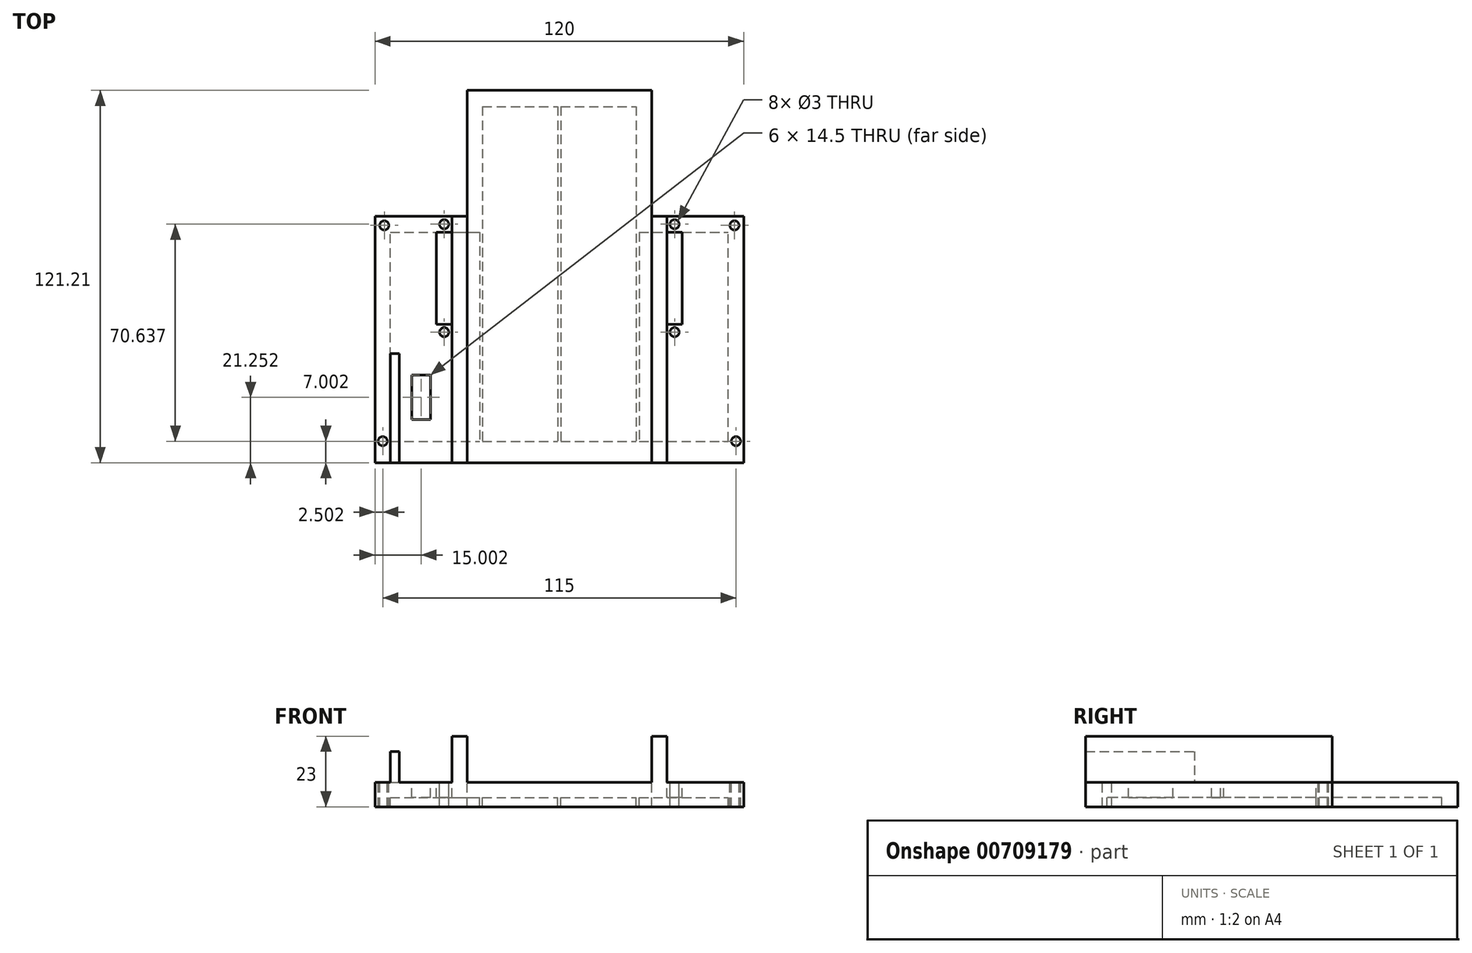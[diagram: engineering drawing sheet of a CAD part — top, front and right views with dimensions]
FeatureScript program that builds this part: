
annotation { "Feature Type Name" : "Feature", "Feature Type Description" : "" }
export const myFeature = defineFeature(function(context is Context, id is Id, definition is map)
    precondition{}
    {
        {
            var Q0;
            Q0=qCreatedBy(makeId("Top.planeOp"),FACE);
            var sketch = newSketch(context, id + "F0", { "sketchPlane" : qUnion([Q0])});
            skLineSegment(sketch, "E0.bottom", {"start": v(-56.52, -50.08) * mm, "end": v(53.48, -50.08) * mm});
            skLineSegment(sketch, "E0.top", {"start": v(-56.52, 17.92) * mm, "end": v(-26.52, 17.92) * mm});
            skLineSegment(sketch, "E0.left", {"start": v(-56.52, -50.08) * mm, "end": v(-56.52, 17.92) * mm});
            skLineSegment(sketch, "E0.right", {"start": v(53.48, -50.08) * mm, "end": v(53.48, 17.92) * mm});
            skLineSegment(sketch, "E1.bottom", {"start": v(-26.52, 58.85) * mm, "end": v(23.48, 58.85) * mm});
            skLineSegment(sketch, "E1.left", {"start": v(-26.52, 58.85) * mm, "end": v(-26.52, 17.92) * mm});
            skLineSegment(sketch, "E1.right", {"start": v(23.48, 58.85) * mm, "end": v(23.48, 17.92) * mm});
            skLineSegment(sketch, "E2.trimOffspring", {"start": v(23.48, 17.92) * mm, "end": v(53.48, 17.92) * mm});
            skCircle(sketch, "E3", {"center": v(55.98, -50.08) * mm, "radius": 1.5 * mm});
            skCircle(sketch, "E4", {"center": v(-59.02, -50.08) * mm, "radius": 1.5 * mm});
            skCircle(sketch, "E5", {"center": v(55.48, 20.18) * mm, "radius": 1.5 * mm});
            skCircle(sketch, "E6", {"center": v(-58.5, 20.19) * mm, "radius": 1.5 * mm});
            skLineSegment(sketch, "E7", {"start": v(-61.52, 23.2) * mm, "end": v(-61.52, -57.08) * mm});
            skLineSegment(sketch, "E8", {"start": v(-61.52, -57.08) * mm, "end": v(58.48, -57.08) * mm});
            skLineSegment(sketch, "E9", {"start": v(58.48, -57.08) * mm, "end": v(58.48, 23.2) * mm});
            skLineSegment(sketch, "E10", {"start": v(58.48, 23.2) * mm, "end": v(28.48, 23.2) * mm});
            skLineSegment(sketch, "E11", {"start": v(28.48, 64.13) * mm, "end": v(-31.52, 64.13) * mm});
            skLineSegment(sketch, "E12", {"start": v(-31.52, 64.13) * mm, "end": v(-31.52, 23.2) * mm});
            skLineSegment(sketch, "E13", {"start": v(-31.52, 23.2) * mm, "end": v(-61.52, 23.2) * mm});
            skLineSegment(sketch, "E14", {"start": v(-31.52, 23.2) * mm, "end": v(-31.52, -57.08) * mm});
            skLineSegment(sketch, "E15", {"start": v(28.48, 23.2) * mm, "end": v(28.48, -57.08) * mm});
            skLineSegment(sketch, "E16", {"start": v(-36.52, 23.2) * mm, "end": v(-36.52, -57.08) * mm});
            skLineSegment(sketch, "E17", {"start": v(-36.52, -57.08) * mm, "end": v(-31.52, -57.08) * mm});
            skLineSegment(sketch, "E18", {"start": v(-36.52, 23.2) * mm, "end": v(-31.52, 23.2) * mm});
            skLineSegment(sketch, "E19", {"start": v(33.48, 23.2) * mm, "end": v(33.48, -57.08) * mm});
            skLineSegment(sketch, "E20", {"start": v(33.48, -57.08) * mm, "end": v(28.48, -57.08) * mm});
            skLineSegment(sketch, "E21.bottom", {"start": v(-43.52, -43.08) * mm, "end": v(-49.52, -43.08) * mm});
            skLineSegment(sketch, "E21.top", {"start": v(-43.52, -28.58) * mm, "end": v(-49.52, -28.58) * mm});
            skLineSegment(sketch, "E21.left", {"start": v(-43.52, -43.08) * mm, "end": v(-43.52, -28.58) * mm});
            skLineSegment(sketch, "E21.right", {"start": v(-49.52, -43.08) * mm, "end": v(-49.52, -28.58) * mm});
            skLineSegment(sketch, "E22.bottom", {"start": v(-56.52, -50.08) * mm, "end": v(-53.58, -50.08) * mm});
            skLineSegment(sketch, "E22.top", {"start": v(-56.52, -21.58) * mm, "end": v(-53.58, -21.58) * mm});
            skLineSegment(sketch, "E22.left", {"start": v(-56.52, -50.08) * mm, "end": v(-56.52, -21.58) * mm});
            skLineSegment(sketch, "E22.right", {"start": v(-53.58, -50.08) * mm, "end": v(-53.58, -21.58) * mm});
            skLineSegment(sketch, "E23", {"start": v(-53.58, -50.08) * mm, "end": v(-53.58, -57.08) * mm});
            skLineSegment(sketch, "E24", {"start": v(-56.52, -50.08) * mm, "end": v(-56.52, -57.08) * mm});
            skLineSegment(sketch, "E25", {"start": v(-53.58, -57.08) * mm, "end": v(-56.52, -57.08) * mm});
            skLineSegment(sketch, "E26.bottom", {"start": v(23.48, 17.92) * mm, "end": v(24.48, 17.92) * mm});
            skLineSegment(sketch, "E26.top", {"start": v(23.48, -50.08) * mm, "end": v(24.48, -50.08) * mm});
            skLineSegment(sketch, "E26.left", {"start": v(23.48, 17.92) * mm, "end": v(23.48, -50.08) * mm});
            skLineSegment(sketch, "E26.right", {"start": v(24.48, 17.92) * mm, "end": v(24.48, -50.08) * mm});
            skLineSegment(sketch, "E27.left", {"start": v(24.48, -50.08) * mm, "end": v(24.48, 17.92) * mm});
            skLineSegment(sketch, "E28.bottom", {"start": v(-26.52, 17.92) * mm, "end": v(-27.52, 17.92) * mm});
            skLineSegment(sketch, "E28.top", {"start": v(-26.52, -50.08) * mm, "end": v(-27.52, -50.08) * mm});
            skLineSegment(sketch, "E28.left", {"start": v(-26.52, 17.92) * mm, "end": v(-26.52, -50.08) * mm});
            skLineSegment(sketch, "E28.right", {"start": v(-27.52, 17.92) * mm, "end": v(-27.52, -50.08) * mm});
            skLineSegment(sketch, "E29", {"start": v(-1.52, 58.85) * mm, "end": v(-2.02, 58.85) * mm});
            skLineSegment(sketch, "E30", {"start": v(-2.02, 58.85) * mm, "end": v(-2.02, -50.08) * mm});
            skLineSegment(sketch, "E31.MirrorCS", {"start": v(-1.02, 58.85) * mm, "end": v(-1.02, -50.08) * mm});
            skLineSegment(sketch, "E32.bottom", {"start": v(33.48, 23.2) * mm, "end": v(28.48, 23.2) * mm});
            skLineSegment(sketch, "E32.right", {"start": v(28.48, 23.2) * mm, "end": v(28.48, 64.13) * mm});
            skLineSegment(sketch, "E33.bottom", {"start": v(38.48, 17.92) * mm, "end": v(33.48, 17.92) * mm});
            skLineSegment(sketch, "E33.top", {"start": v(38.48, -12.08) * mm, "end": v(33.48, -12.08) * mm});
            skLineSegment(sketch, "E33.left", {"start": v(38.48, 17.92) * mm, "end": v(38.48, -12.08) * mm});
            skLineSegment(sketch, "E33.right", {"start": v(33.48, 17.92) * mm, "end": v(33.48, -12.08) * mm});
            skLineSegment(sketch, "E34.right", {"start": v(33.48, 17.92) * mm, "end": v(33.48, 23.2) * mm});
            skLineSegment(sketch, "E35.right", {"start": v(33.48, -12.08) * mm, "end": v(33.48, -17.08) * mm});
            skPoint(sketch, "E36", {"position": v(35.98, 20.56) * mm});
            skPoint(sketch, "E37", {"position": v(35.98, -14.58) * mm});
            skPoint(sketch, "E38.MirrorP", {"position": v(-39.02, -14.58) * mm});
            skPoint(sketch, "E39.MirrorP", {"position": v(-39.02, 20.56) * mm});
            skLineSegment(sketch, "E40.MirrorCS", {"start": v(-41.52, 17.92) * mm, "end": v(-41.52, -12.08) * mm});
            skLineSegment(sketch, "E41.MirrorCS", {"start": v(-41.52, -12.08) * mm, "end": v(-36.52, -12.08) * mm});
            skSolve(sketch);
        }
        {
            var Q0;
            {var subQ0=sQuery(id+"F0.wireOp",EDGE,"E28.right");var subQ6=sQuery(id+"F0.wireOp",EDGE,"E26.right");Q0=qUnion([makeQuery(id+"F0.imprint","IMPRINT",FACE,{"disambiguationData":[TD([[makeQuery(id+"F0.imprint","IMPRINT",EDGE,{"derivedFrom":subQ6}),1.0]])]}),makeQuery(id+"F0.imprint","IMPRINT",FACE,{"disambiguationData":[TD([[makeQuery(id+"F0.imprint","IMPRINT",EDGE,{"derivedFrom":subQ0}),-1.0]])]})]);}
            var Q1;
            Q1=makeQuery(id+"F0.imprint","IMPRINT",FACE,{"disambiguationData":[TD([[makeQuery(id+"F0.imprint","IMPRINT",EDGE,{"derivedFrom":sQuery(id+"F0.wireOp",EDGE,"E21.bottom")}),1.0]])]});
            var Q2;
            {var subQ4=sQuery(id+"F0.wireOp",EDGE,"E22.top");Q2=makeQuery(id+"F0.imprint","IMPRINT",FACE,{"disambiguationData":[TD([[makeQuery(id+"F0.imprint","IMPRINT",EDGE,{"derivedFrom":subQ4}),-1.0]])]});}
            var Q3;
            {var subQ0=sQuery(id+"F0.wireOp",EDGE,"E28.left");Q3=makeQuery(id+"F0.imprint","IMPRINT",FACE,{"disambiguationData":[TD([[makeQuery(id+"F0.imprint","IMPRINT",EDGE,{"derivedFrom":subQ0}),-1.0]])]});}
            var Q4;
            {var subQ0=sQuery(id+"F0.wireOp",EDGE,"E1.left");var subQ2=sQuery(id+"F0.wireOp",EDGE,"E30");var subQ7=makeQuery(id+"F0.imprint","IMPRINT",EDGE,{"derivedFrom":subQ2});var subQ9=sQuery(id+"F0.wireOp",EDGE,"E1.right");Q4=qUnion([makeQuery(id+"F0.imprint","IMPRINT",FACE,{"disambiguationData":[TD([[subQ7,1.0]])]}),makeQuery(id+"F0.imprint","IMPRINT",FACE,{"disambiguationData":[TD([[makeQuery(id+"F0.imprint","IMPRINT",EDGE,{"derivedFrom":subQ9}),-1.0]])]}),makeQuery(id+"F0.imprint","IMPRINT",FACE,{"disambiguationData":[TD([[makeQuery(id+"F0.imprint","IMPRINT",EDGE,{"derivedFrom":subQ0}),1.0]])]})]);}
            var Q5;
            {var subQ0=sQuery(id+"F0.wireOp",EDGE,"E26.left");Q5=makeQuery(id+"F0.imprint","IMPRINT",FACE,{"disambiguationData":[TD([[makeQuery(id+"F0.imprint","IMPRINT",EDGE,{"derivedFrom":subQ0}),1.0]])]});}
            var Q6;
            {var subQ5=sQuery(id+"F0.wireOp",EDGE,"E0.right");Q6=makeQuery(id+"F0.imprint","IMPRINT",FACE,{"disambiguationData":[TD([[makeQuery(id+"F0.imprint","IMPRINT",EDGE,{"derivedFrom":subQ5}),1.0]])]});}
            var Q7;
            {var subQ0=sQuery(id+"F0.wireOp",EDGE,"E19");var subQ1=makeQuery(id+"F0.imprint","IMPRINT",VERTEX,{"derivedFrom":subQ0});Q7=makeQuery(id+"F0.imprint","IMPRINT",FACE,{"disambiguationData":[TD([[makeQuery(id+"F0.imprint","IMPRINT",EDGE,{"disambiguationData":[TD([[subQ1,-1.0]])],"derivedFrom":subQ0}),-1.0]])]});}
            var Q8;
            Q8=makeQuery(id+"F0.imprint","IMPRINT",FACE,{"disambiguationData":[TD([[makeQuery(id+"F0.imprint","IMPRINT",EDGE,{"derivedFrom":sQuery(id+"F0.wireOp",EDGE,"E33.bottom")}),1.0]])]});
            var Q9;
            {var subQ0=sQuery(id+"F0.wireOp",EDGE,"E16");var subQ2=sQuery(id+"F0.wireOp",EDGE,"E0.bottom");var subQ3=makeQuery(id+"F0.imprint","INTERSECT",VERTEX,{"derivedFrom":[subQ2,subQ0]});Q9=makeQuery(id+"F0.imprint","IMPRINT",FACE,{"disambiguationData":[TD([[makeQuery(id+"F0.imprint","IMPRINT",EDGE,{"disambiguationData":[TD([[subQ3,-1.0]])],"derivedFrom":subQ2}),1.0]])]});}
            var Q10;
            Q10=sQuery(id+"F0.wireOp",EDGE,"E7");
            var Q11;
            Q11=sQuery(id+"F0.wireOp",EDGE,"E0.top");
            var Q12;
            Q12=sQuery(id+"F0.wireOp",EDGE,"E1.right");
            var Q13;
            Q13=sQuery(id+"F0.wireOp",EDGE,"E13");
            var Q14;
            Q14=sQuery(id+"F0.wireOp",EDGE,"E0.left");
            var Q15;
            Q15=sQuery(id+"F0.wireOp",EDGE,"E8");
            var Q16;
            Q16=sQuery(id+"F0.wireOp",EDGE,"E2.trimOffspring");
            var Q17;
            Q17=sQuery(id+"F0.wireOp",EDGE,"E0.bottom");
            var Q18;
            Q18=sQuery(id+"F0.wireOp",EDGE,"E9");
            var Q19;
            Q19=sQuery(id+"F0.wireOp",EDGE,"E10");
            var Q20;
            Q20=sQuery(id+"F0.wireOp",EDGE,"E1.left");
            var Q21;
            Q21=sQuery(id+"F0.wireOp",EDGE,"E1.bottom");
            var Q22;
            Q22=sQuery(id+"F0.wireOp",EDGE,"5a019d25-20b0-43ed-8b83-62d001f18063");
            var Q23;
            Q23=sQuery(id+"F0.wireOp",EDGE,"E0.right");
            var Q24;
            Q24=sQuery(id+"F0.wireOp",EDGE,"E12");
            var Q25;
            Q25=sQuery(id+"F0.wireOp",EDGE,"E11");
            var Q26;
            Q26=sQuery(id+"F0.wireOp",EDGE,"E4");
            var Q27;
            Q27=sQuery(id+"F0.wireOp",EDGE,"E3");
            var Q28;
            Q28=sQuery(id+"F0.wireOp",EDGE,"E5");
            var Q29;
            Q29=sQuery(id+"F0.wireOp",EDGE,"E6");
            extrude(context, id + "F1", {"entities" : qUnion([Q0, Q1, Q2, Q3, Q4, Q5, Q6, Q7, Q8, Q9]), "surfaceEntities" : qUnion([Q10, Q11, Q12, Q13, Q14, Q15, Q16, Q17, Q18, Q19, Q20, Q21, Q22, Q23, Q24, Q25, Q26, Q27, Q28, Q29]), "oppositeDirection" : true, "depth" : 5 * mm, "offsetDistance" : 25 * mm});
        }
        {
            var Q0;
            {var subQ0=sQuery(id+"F0.wireOp",EDGE,"E0.bottom");var subQ11=makeQuery(id+"F0.imprint","INTERSECT",VERTEX,{"derivedFrom":[subQ0,sQuery(id+"F0.wireOp",EDGE,"E28.left")]});Q0=makeQuery(id+"F0.imprint","IMPRINT",FACE,{"disambiguationData":[TD([[makeQuery(id+"F0.imprint","IMPRINT",EDGE,{"disambiguationData":[TD([[subQ11,-1.0]])],"derivedFrom":subQ0}),-1.0]])]});}
            var Q1;
            Q1=makeQuery(id+"F0.imprint","IMPRINT",FACE,{"disambiguationData":[TD([[makeQuery(id+"F0.imprint","IMPRINT",EDGE,{"derivedFrom":sQuery(id+"F0.wireOp",EDGE,"E4")}),-1.0]])]});
            var Q2;
            {var subQ8=sQuery(id+"F0.wireOp",EDGE,"E0.right");Q2=makeQuery(id+"F0.imprint","IMPRINT",FACE,{"disambiguationData":[TD([[makeQuery(id+"F0.imprint","IMPRINT",EDGE,{"derivedFrom":subQ8}),-1.0]])]});}
            var Q3;
            {var subQ5=sQuery(id+"F0.wireOp",EDGE,"LNSsdfv9-6JXA-3CWA-gpuE-UEZ15CtiGnE0");Q3=makeQuery(id+"F0.imprint","IMPRINT",FACE,{"disambiguationData":[TD([[makeQuery(id+"F0.imprint","IMPRINT",EDGE,{"derivedFrom":subQ5}),-1.0]])]});}
            var Q4;
            {var subQ5=sQuery(id+"F0.wireOp",EDGE,"E18");Q4=makeQuery(id+"F0.imprint","IMPRINT",FACE,{"disambiguationData":[TD([[makeQuery(id+"F0.imprint","IMPRINT",EDGE,{"derivedFrom":subQ5}),-1.0]])]});}
            var Q5;
            {var subQ0=sQuery(id+"F0.wireOp",EDGE,"E23");Q5=makeQuery(id+"F0.imprint","IMPRINT",FACE,{"disambiguationData":[TD([[makeQuery(id+"F0.imprint","IMPRINT",EDGE,{"derivedFrom":subQ0}),-1.0]])]});}
            var Q6;
            {var subQ0=sQuery(id+"F0.wireOp",EDGE,"E23");Q6=makeQuery(id+"F0.imprint","IMPRINT",FACE,{"disambiguationData":[TD([[makeQuery(id+"F0.imprint","IMPRINT",EDGE,{"derivedFrom":subQ0}),1.0]])]});}
            var Q7;
            {var subQ0=sQuery(id+"F0.wireOp",EDGE,"E16");var subQ1=sQuery(id+"F0.wireOp",EDGE,"E0.bottom");var subQ2=makeQuery(id+"F0.imprint","INTERSECT",VERTEX,{"derivedFrom":[subQ1,subQ0]});Q7=makeQuery(id+"F0.imprint","IMPRINT",FACE,{"disambiguationData":[TD([[makeQuery(id+"F0.imprint","IMPRINT",EDGE,{"disambiguationData":[TD([[subQ2,-1.0]])],"derivedFrom":subQ1}),-1.0]])]});}
            var Q8;
            {var subQ0=sQuery(id+"F0.wireOp",EDGE,"E19");var subQ1=sQuery(id+"F0.wireOp",EDGE,"E0.bottom");var subQ2=makeQuery(id+"F0.imprint","INTERSECT",VERTEX,{"derivedFrom":[subQ1,subQ0]});Q8=makeQuery(id+"F0.imprint","IMPRINT",FACE,{"disambiguationData":[TD([[makeQuery(id+"F0.imprint","IMPRINT",EDGE,{"disambiguationData":[TD([[subQ2,1.0]])],"derivedFrom":subQ1}),-1.0]])]});}
            var Q9;
            {var subQ0=sQuery(id+"F0.wireOp",EDGE,"E28.left");Q9=makeQuery(id+"F0.imprint","IMPRINT",FACE,{"disambiguationData":[TD([[makeQuery(id+"F0.imprint","IMPRINT",EDGE,{"derivedFrom":subQ0}),-1.0]])]});}
            var Q10;
            {var subQ0=sQuery(id+"F0.wireOp",EDGE,"E26.left");Q10=makeQuery(id+"F0.imprint","IMPRINT",FACE,{"disambiguationData":[TD([[makeQuery(id+"F0.imprint","IMPRINT",EDGE,{"derivedFrom":subQ0}),1.0]])]});}
            var Q11;
            {var subQ2=sQuery(id+"F0.wireOp",EDGE,"E30");Q11=makeQuery(id+"F0.imprint","IMPRINT",FACE,{"disambiguationData":[TD([[makeQuery(id+"F0.imprint","IMPRINT",EDGE,{"derivedFrom":subQ2}),1.0]])]});}
            var Q12;
            {var subQ0=sQuery(id+"F0.wireOp",EDGE,"E15");var subQ1=sQuery(id+"F0.wireOp",EDGE,"E2.trimOffspring");var subQ2=makeQuery(id+"F0.imprint","INTERSECT",VERTEX,{"derivedFrom":[subQ1,subQ0]});Q12=makeQuery(id+"F0.imprint","IMPRINT",FACE,{"disambiguationData":[TD([[makeQuery(id+"F0.imprint","IMPRINT",EDGE,{"disambiguationData":[TD([[subQ2,-1.0]])],"derivedFrom":subQ1}),1.0]])]});}
            var Q13;
            {var subQ0=sQuery(id+"F0.wireOp",EDGE,"E14");var subQ1=sQuery(id+"F0.wireOp",EDGE,"E0.top");var subQ2=makeQuery(id+"F0.imprint","INTERSECT",VERTEX,{"derivedFrom":[subQ1,subQ0]});Q13=makeQuery(id+"F0.imprint","IMPRINT",FACE,{"disambiguationData":[TD([[makeQuery(id+"F0.imprint","IMPRINT",EDGE,{"disambiguationData":[TD([[subQ2,1.0]])],"derivedFrom":subQ1}),1.0]])]});}
            var Q14;
            {var subQ9=sQuery(id+"F0.wireOp",EDGE,"E1.left");Q14=makeQuery(id+"F0.imprint","IMPRINT",FACE,{"disambiguationData":[TD([[makeQuery(id+"F0.imprint","IMPRINT",EDGE,{"derivedFrom":subQ9}),-1.0]])]});}
            var Q15;
            Q15=makeQuery(id+"F0.imprint","IMPRINT",FACE,{"disambiguationData":[TD([[makeQuery(id+"F0.imprint","IMPRINT",EDGE,{"derivedFrom":sQuery(id+"F0.wireOp",EDGE,"E32.bottom")}),-1.0]])]});
            var Q16;
            Q16=makeQuery(id+"F0.imprint","IMPRINT",FACE,{"disambiguationData":[TD([[makeQuery(id+"F0.imprint","IMPRINT",EDGE,{"derivedFrom":sQuery(id+"F0.wireOp",EDGE,"E18")}),1.0]])]});
            extrude(context, id + "F2", {"entities" : qUnion([Q0, Q1, Q2, Q3, Q4, Q5, Q6, Q7, Q8, Q9, Q10, Q11, Q12, Q13, Q14, Q15, Q16]), "operationType" : NewBodyOperationType.ADD, "oppositeDirection" : true, "depth" : 8 * mm, "offsetDistance" : 25 * mm});
        }
        {
            var Q0;
            {var subQ0=sQuery(id+"F0.wireOp",EDGE,"E19");var subQ1=makeQuery(id+"F0.imprint","IMPRINT",VERTEX,{"derivedFrom":subQ0});Q0=makeQuery(id+"F0.imprint","IMPRINT",FACE,{"disambiguationData":[TD([[makeQuery(id+"F0.imprint","IMPRINT",EDGE,{"disambiguationData":[TD([[subQ1,-1.0]])],"derivedFrom":subQ0}),-1.0]])]});}
            var Q1;
            {var subQ5=sQuery(id+"F0.wireOp",EDGE,"E18");Q1=makeQuery(id+"F0.imprint","IMPRINT",FACE,{"disambiguationData":[TD([[makeQuery(id+"F0.imprint","IMPRINT",EDGE,{"derivedFrom":subQ5}),-1.0]])]});}
            var Q2;
            {var subQ0=sQuery(id+"F0.wireOp",EDGE,"E16");var subQ1=sQuery(id+"F0.wireOp",EDGE,"E0.bottom");var subQ2=makeQuery(id+"F0.imprint","INTERSECT",VERTEX,{"derivedFrom":[subQ1,subQ0]});Q2=makeQuery(id+"F0.imprint","IMPRINT",FACE,{"disambiguationData":[TD([[makeQuery(id+"F0.imprint","IMPRINT",EDGE,{"disambiguationData":[TD([[subQ2,-1.0]])],"derivedFrom":subQ1}),-1.0]])]});}
            var Q3;
            {var subQ5=sQuery(id+"F0.wireOp",EDGE,"LNSsdfv9-6JXA-3CWA-gpuE-UEZ15CtiGnE0");Q3=makeQuery(id+"F0.imprint","IMPRINT",FACE,{"disambiguationData":[TD([[makeQuery(id+"F0.imprint","IMPRINT",EDGE,{"derivedFrom":subQ5}),-1.0]])]});}
            var Q4;
            {var subQ0=sQuery(id+"F0.wireOp",EDGE,"E19");var subQ1=sQuery(id+"F0.wireOp",EDGE,"E0.bottom");var subQ2=makeQuery(id+"F0.imprint","INTERSECT",VERTEX,{"derivedFrom":[subQ1,subQ0]});Q4=makeQuery(id+"F0.imprint","IMPRINT",FACE,{"disambiguationData":[TD([[makeQuery(id+"F0.imprint","IMPRINT",EDGE,{"disambiguationData":[TD([[subQ2,1.0]])],"derivedFrom":subQ1}),-1.0]])]});}
            var Q5;
            {var subQ0=sQuery(id+"F0.wireOp",EDGE,"E15");var subQ1=sQuery(id+"F0.wireOp",EDGE,"E2.trimOffspring");var subQ2=makeQuery(id+"F0.imprint","INTERSECT",VERTEX,{"derivedFrom":[subQ1,subQ0]});Q5=makeQuery(id+"F0.imprint","IMPRINT",FACE,{"disambiguationData":[TD([[makeQuery(id+"F0.imprint","IMPRINT",EDGE,{"disambiguationData":[TD([[subQ2,-1.0]])],"derivedFrom":subQ1}),1.0]])]});}
            var Q6;
            {var subQ0=sQuery(id+"F0.wireOp",EDGE,"E14");var subQ1=sQuery(id+"F0.wireOp",EDGE,"E0.top");var subQ2=makeQuery(id+"F0.imprint","INTERSECT",VERTEX,{"derivedFrom":[subQ1,subQ0]});Q6=makeQuery(id+"F0.imprint","IMPRINT",FACE,{"disambiguationData":[TD([[makeQuery(id+"F0.imprint","IMPRINT",EDGE,{"disambiguationData":[TD([[subQ2,1.0]])],"derivedFrom":subQ1}),1.0]])]});}
            var Q7;
            Q7=makeQuery(id+"F0.imprint","IMPRINT",FACE,{"disambiguationData":[TD([[makeQuery(id+"F0.imprint","IMPRINT",EDGE,{"derivedFrom":sQuery(id+"F0.wireOp",EDGE,"E32.bottom")}),-1.0]])]});
            var Q8;
            Q8=makeQuery(id+"F0.imprint","IMPRINT",FACE,{"disambiguationData":[TD([[makeQuery(id+"F0.imprint","IMPRINT",EDGE,{"derivedFrom":sQuery(id+"F0.wireOp",EDGE,"E18")}),1.0]])]});
            var Q9;
            {var subQ0=sQuery(id+"F0.wireOp",EDGE,"E16");var subQ2=sQuery(id+"F0.wireOp",EDGE,"E0.bottom");var subQ3=makeQuery(id+"F0.imprint","INTERSECT",VERTEX,{"derivedFrom":[subQ2,subQ0]});Q9=makeQuery(id+"F0.imprint","IMPRINT",FACE,{"disambiguationData":[TD([[makeQuery(id+"F0.imprint","IMPRINT",EDGE,{"disambiguationData":[TD([[subQ3,-1.0]])],"derivedFrom":subQ2}),1.0]])]});}
            extrude(context, id + "F3", {"entities" : qUnion([Q0, Q1, Q2, Q3, Q4, Q5, Q6, Q7, Q8, Q9]), "operationType" : NewBodyOperationType.ADD, "depth" : 15 * mm, "offsetDistance" : 25 * mm});
        }
        {
            var Q0;
            {var subQ4=sQuery(id+"F0.wireOp",EDGE,"E22.top");Q0=makeQuery(id+"F0.imprint","IMPRINT",FACE,{"disambiguationData":[TD([[makeQuery(id+"F0.imprint","IMPRINT",EDGE,{"derivedFrom":subQ4}),-1.0]])]});}
            var Q1;
            {var subQ0=sQuery(id+"F0.wireOp",EDGE,"E23");Q1=makeQuery(id+"F0.imprint","IMPRINT",FACE,{"disambiguationData":[TD([[makeQuery(id+"F0.imprint","IMPRINT",EDGE,{"derivedFrom":subQ0}),-1.0]])]});}
            extrude(context, id + "F4", {"entities" : qUnion([Q0, Q1]), "operationType" : NewBodyOperationType.ADD, "depth" : 10 * mm, "offsetDistance" : 25 * mm});
        }
        {
            var Q0;
            Q0=sQuery(id+"F0.wireOp",VERTEX,"E36");
            var Q1;
            Q1=sQuery(id+"F0.wireOp",VERTEX,"E37");
            var Q2;
            Q2=sQuery(id+"F0.wireOp",VERTEX,"E39.MirrorP");
            var Q3;
            Q3=sQuery(id+"F0.wireOp",VERTEX,"E38.MirrorP");
            var Q4;
            Q4=makeQuery(id+"F1.opExtrude","SWEPT_BODY",BODY,{"disambiguationData":[OSD([sQuery(id+"F0.wireOp",EDGE,"E0.bottom"),sQuery(id+"F0.wireOp",EDGE,"E0.top"),sQuery(id+"F0.wireOp",EDGE,"E0.left"),sQuery(id+"F0.wireOp",EDGE,"E0.right"),sQuery(id+"F0.wireOp",EDGE,"E1.bottom"),sQuery(id+"F0.wireOp",EDGE,"E1.left"),sQuery(id+"F0.wireOp",EDGE,"E1.right"),sQuery(id+"F0.wireOp",EDGE,"E2.trimOffspring"),sQuery(id+"F0.wireOp",EDGE,"E16"),sQuery(id+"F0.wireOp",EDGE,"E19"),sQuery(id+"F0.wireOp",EDGE,"E21.bottom"),sQuery(id+"F0.wireOp",EDGE,"E21.top"),sQuery(id+"F0.wireOp",EDGE,"E21.left"),sQuery(id+"F0.wireOp",EDGE,"E21.right"),sQuery(id+"F0.wireOp",EDGE,"E33.top"),sQuery(id+"F0.wireOp",EDGE,"E33.left"),sQuery(id+"F0.wireOp",EDGE,"E40.MirrorCS"),sQuery(id+"F0.wireOp",EDGE,"E41.MirrorCS")])]});
            hole(context, id + "F5", {"style" : HoleStyle.SIMPLE, "endStyle" : HoleEndStyle.THROUGH, "holeDiameter" : 3 * mm, "majorDiameter" : 5 * mm, "isTappedThrough" : true, "tappedDepth" : 12 * mm, "tapClearance" : 3, "locations" : qUnion([Q0, Q1, Q2, Q3]), "scope" : qUnion([Q4])});
        }
    });
